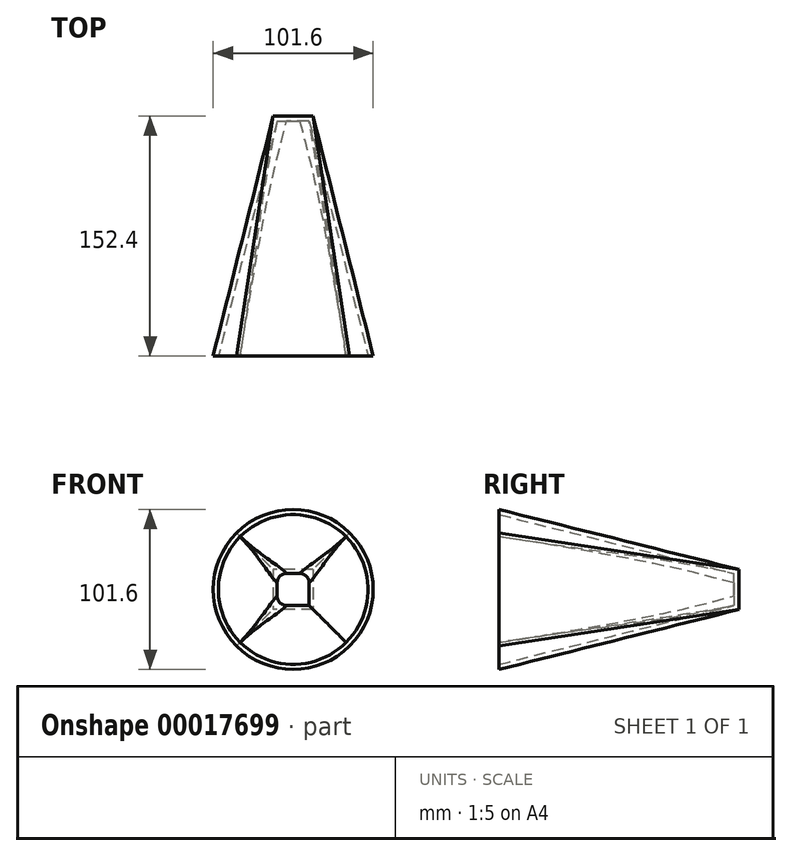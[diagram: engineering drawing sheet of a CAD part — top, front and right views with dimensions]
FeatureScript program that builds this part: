
annotation { "Feature Type Name" : "Feature", "Feature Type Description" : "" }
export const myFeature = defineFeature(function(context is Context, id is Id, definition is map)
    precondition{}
    {
        {
            var Q0;
            Q0=qCreatedBy(makeId("Front.planeOp"),FACE);
            var sketch = newSketch(context, id + "F0", { "sketchPlane" : qUnion([Q0])});
            skLineSegment(sketch, "E0.rect.bottom", {"start": v(12.7, 12.7) * mm, "end": v(-12.7, 12.7) * mm});
            skLineSegment(sketch, "E0.rect.top", {"start": v(12.7, -12.7) * mm, "end": v(-12.7, -12.7) * mm});
            skLineSegment(sketch, "E0.rect.left", {"start": v(12.7, 12.7) * mm, "end": v(12.7, -12.7) * mm});
            skLineSegment(sketch, "E0.rect.right", {"start": v(-12.7, 12.7) * mm, "end": v(-12.7, -12.7) * mm});
            skPoint(sketch, "E0.rect.middle", {"position": v(0, 0) * mm});
            skSolve(sketch);
        }
        {
            var Q0;
            Q0=qCreatedBy(makeId("Front.planeOp"),FACE);
            cPlane(context, id + "F1", {"entities" : qUnion([Q0]), "cplaneType" : CPlaneType.OFFSET, "offset" : 152.4 * mm, "width" : 152.4 * mm, "height" : 152.4 * mm});
        }
        {
            var Q0;
            Q0=qCreatedBy(id+"F1.planeOp",FACE);
            var sketch = newSketch(context, id + "F2", { "sketchPlane" : qUnion([Q0])});
            skCircle(sketch, "E1", {"center": v(0, 0) * mm, "radius": 50.8 * mm});
            skSolve(sketch);
        }
        {
            var Q0;
            Q0=makeQuery(id+"F2.imprint","IMPRINT",FACE,{"disambiguationData":[TD([[makeQuery(id+"F2.imprint","IMPRINT",EDGE,{"derivedFrom":sQuery(id+"F2.wireOp",EDGE,"E1")}),1.0]])]});
            var Q1;
            Q1=makeQuery(id+"F0.imprint","IMPRINT",FACE,{"disambiguationData":[TD([[makeQuery(id+"F0.imprint","IMPRINT",EDGE,{"derivedFrom":sQuery(id+"F0.wireOp",EDGE,"E0.rect.bottom")}),1.0]])]});
            loft(context, id + "F3", {"sheetProfilesArray" : [{ "sheetProfileEntities" : qUnion([Q0]) }, { "sheetProfileEntities" : qUnion([Q1]) }]});
        }
        {
            var Q0;
            Q0=makeQuery(id+"F3.opLoft","CAP_FACE",FACE,{"disambiguationData":[OSD([makeQuery(id+"F2.imprint","IMPRINT",FACE,{"disambiguationData":[TD([[makeQuery(id+"F2.imprint","IMPRINT",EDGE,{"derivedFrom":sQuery(id+"F2.wireOp",EDGE,"E1")}),1.0]])]})])],"isStart":true});
            shell(context, id + "F4", {"entities" : qUnion([Q0]), "thickness" : 3.17 * mm});
        }
        {
            var Q0;
            Q0=makeQuery(id+"F4.opShell","OFFSET_EDGE",EDGE,{"disambiguationData":[OSD([sQuery(id+"F0.wireOp",EDGE,"E0.rect.bottom"),sQuery(id+"F0.wireOp",EDGE,"E0.rect.top"),sQuery(id+"F0.wireOp",EDGE,"E0.rect.right"),sQuery(id+"F2.wireOp",EDGE,"E1")])]});
            var Q1;
            Q1=makeQuery(id+"F4.opShell","OFFSET_EDGE",EDGE,{"disambiguationData":[OSD([sQuery(id+"F0.wireOp",EDGE,"E0.rect.bottom"),sQuery(id+"F0.wireOp",EDGE,"E0.rect.left")])]});
            var Q2;
            {var subQ0=sQuery(id+"F0.wireOp",EDGE,"E0.rect.top");var subQ1=sQuery(id+"F0.wireOp",EDGE,"E0.rect.left");var subQ2=sQuery(id+"F0.wireOp",EDGE,"E0.rect.right");var subQ3=sQuery(id+"F2.wireOp",EDGE,"E1");Q2=makeQuery(id+"F4.opShell","OFFSET_EDGE",EDGE,{"disambiguationData":[OSD([subQ0,subQ1,subQ2,subQ3]),TDD([makeQuery(id+"F3.opLoft","SWEPT_EDGE",EDGE,{"disambiguationData":[OSD([subQ0,subQ1,subQ2,subQ3])]})])]});}
            var Q3;
            {var subQ0=sQuery(id+"F0.wireOp",EDGE,"E0.rect.bottom");var subQ1=sQuery(id+"F0.wireOp",EDGE,"E0.rect.top");var subQ2=sQuery(id+"F0.wireOp",EDGE,"E0.rect.left");var subQ3=sQuery(id+"F2.wireOp",EDGE,"E1");Q3=makeQuery(id+"F4.opShell","OFFSET_EDGE",EDGE,{"disambiguationData":[OSD([subQ0,subQ1,subQ2,subQ3]),TDD([makeQuery(id+"F3.opLoft","SWEPT_EDGE",EDGE,{"disambiguationData":[OSD([subQ0,subQ1,subQ2,subQ3])]})])]});}
            fillet(context, id + "F5", {"entities" : qUnion([Q0, Q1, Q2, Q3]), "radius" : 6.35 * mm, "tangentPropagation" : true, "allowEdgeOverflow" : false});
        }
    });
